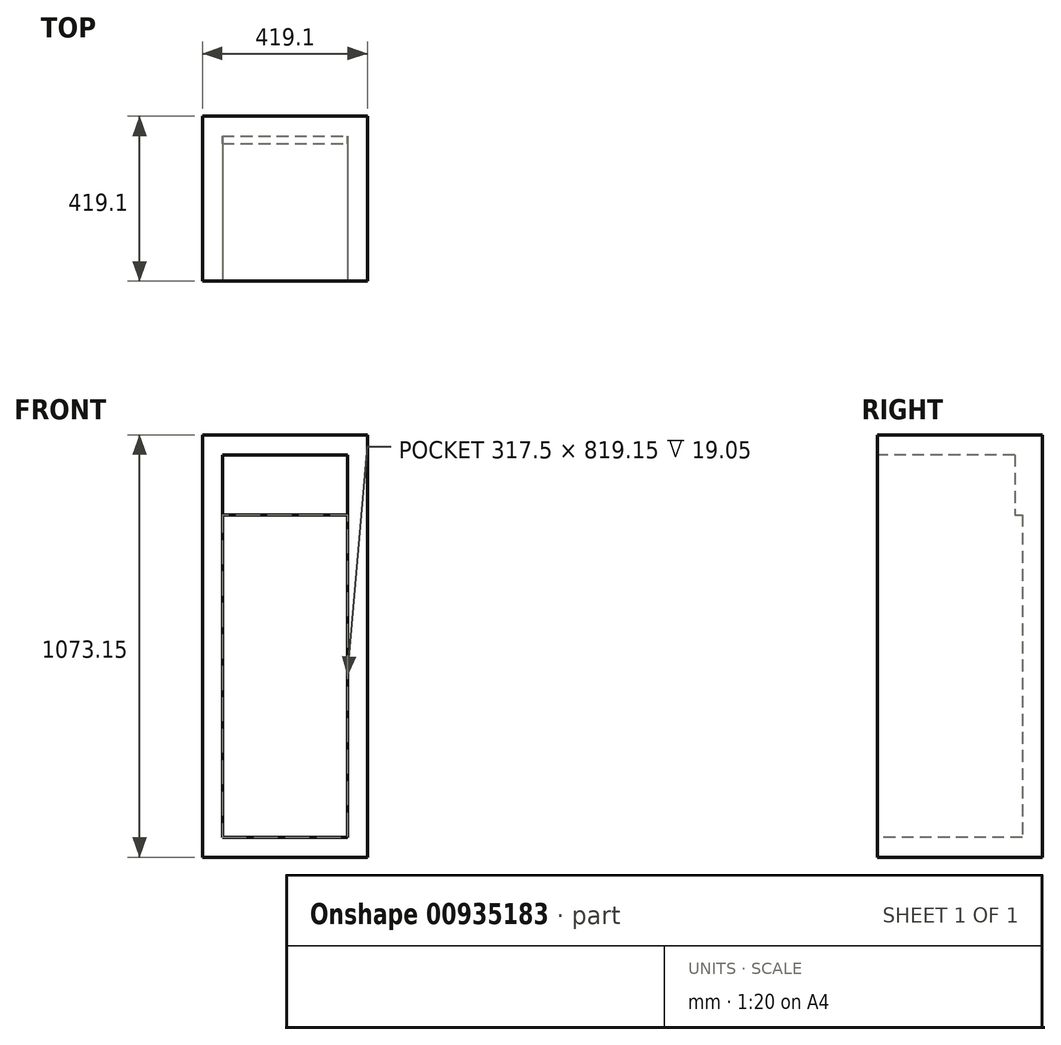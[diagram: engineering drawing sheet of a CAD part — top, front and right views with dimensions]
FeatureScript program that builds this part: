
annotation { "Feature Type Name" : "Feature", "Feature Type Description" : "" }
export const myFeature = defineFeature(function(context is Context, id is Id, definition is map)
    precondition{}
    {
        {
            var Q0;
            Q0=qCreatedBy(makeId("Top.planeOp"),FACE);
            var sketch = newSketch(context, id + "F0", { "sketchPlane" : qUnion([Q0])});
            skLineSegment(sketch, "E0.bottom", {"start": v(-208.6, 268.98) * mm, "end": v(210.5, 268.98) * mm});
            skLineSegment(sketch, "E0.top", {"start": v(-208.6, -150.12) * mm, "end": v(210.5, -150.12) * mm});
            skLineSegment(sketch, "E0.left", {"start": v(-208.6, 268.98) * mm, "end": v(-208.6, -150.12) * mm});
            skLineSegment(sketch, "E0.right", {"start": v(210.5, 268.98) * mm, "end": v(210.5, -150.12) * mm});
            skSolve(sketch);
        }
        {
            var Q0;
            Q0 = qSketchRegion(id + "F0", true);
            extrude(context, id + "F1", {"entities" : qUnion([Q0]), "depth" : 1073.15 * mm, "offsetDistance" : 25.4 * mm});
        }
        {
            var Q0;
            Q0=makeQuery(id+"F1.opExtrude","SWEPT_FACE",FACE,{"disambiguationData":[OSD([sQuery(id+"F0.wireOp",EDGE,"E0.top")])]});
            shell(context, id + "F2", {"entities" : qUnion([Q0]), "thickness" : 50.8 * mm});
        }
        {
            var Q0;
            Q0=makeQuery(id+"F2.opShell","OFFSET_FACE",FACE,{"disambiguationData":[OSD([sQuery(id+"F0.wireOp",EDGE,"E0.bottom")])]});
            var sketch = newSketch(context, id + "F3", { "sketchPlane" : qUnion([Q0])});
            skLineSegment(sketch, "E1.bottom", {"start": v(-157.8, 1022.35) * mm, "end": v(159.7, 1022.35) * mm});
            skLineSegment(sketch, "E1.top", {"start": v(-157.8, 869.95) * mm, "end": v(159.7, 869.95) * mm});
            skLineSegment(sketch, "E1.left", {"start": v(-157.8, 1022.35) * mm, "end": v(-157.8, 869.95) * mm});
            skLineSegment(sketch, "E1.right", {"start": v(159.7, 1022.35) * mm, "end": v(159.7, 869.95) * mm});
            skSolve(sketch);
        }
        {
            var Q0;
            Q0=makeQuery(id+"F3.imprint","IMPRINT",FACE,{"disambiguationData":[TD([[makeQuery(id+"F3.imprint","IMPRINT",EDGE,{"derivedFrom":sQuery(id+"F3.wireOp",EDGE,"E1.bottom")}),-1.0]])]});
            extrude(context, id + "F4", {"entities" : qUnion([Q0]), "operationType" : NewBodyOperationType.ADD, "depth" : 19.05 * mm, "offsetDistance" : 25.4 * mm});
        }
    });
